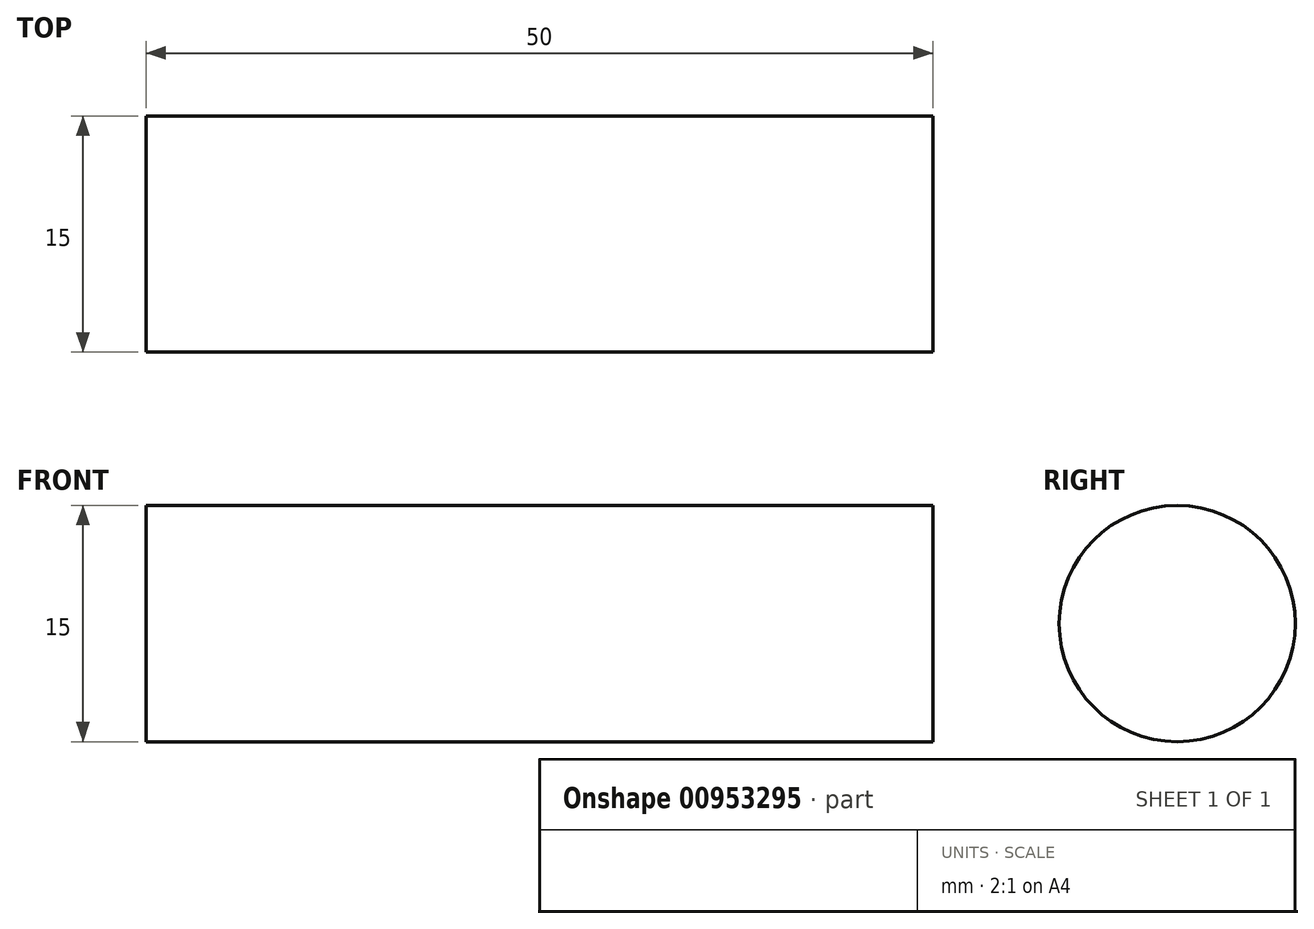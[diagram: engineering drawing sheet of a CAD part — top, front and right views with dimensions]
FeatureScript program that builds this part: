
annotation { "Feature Type Name" : "Feature", "Feature Type Description" : "" }
export const myFeature = defineFeature(function(context is Context, id is Id, definition is map)
    precondition{}
    {
        {
            var Q0;
            Q0=qCreatedBy(makeId("Right.planeOp"),FACE);
            var sketch = newSketch(context, id + "F0", { "sketchPlane" : qUnion([Q0])});
            skCircle(sketch, "E0", {"center": v(0, 0) * mm, "radius": 7.5 * mm});
            skSolve(sketch);
        }
        {
            var Q0;
            Q0 = qSketchRegion(id + "F0", true);
            extrude(context, id + "F1", {"entities" : qUnion([Q0]), "depth" : 50 * mm, "offsetDistance" : 25 * mm});
        }
    });
